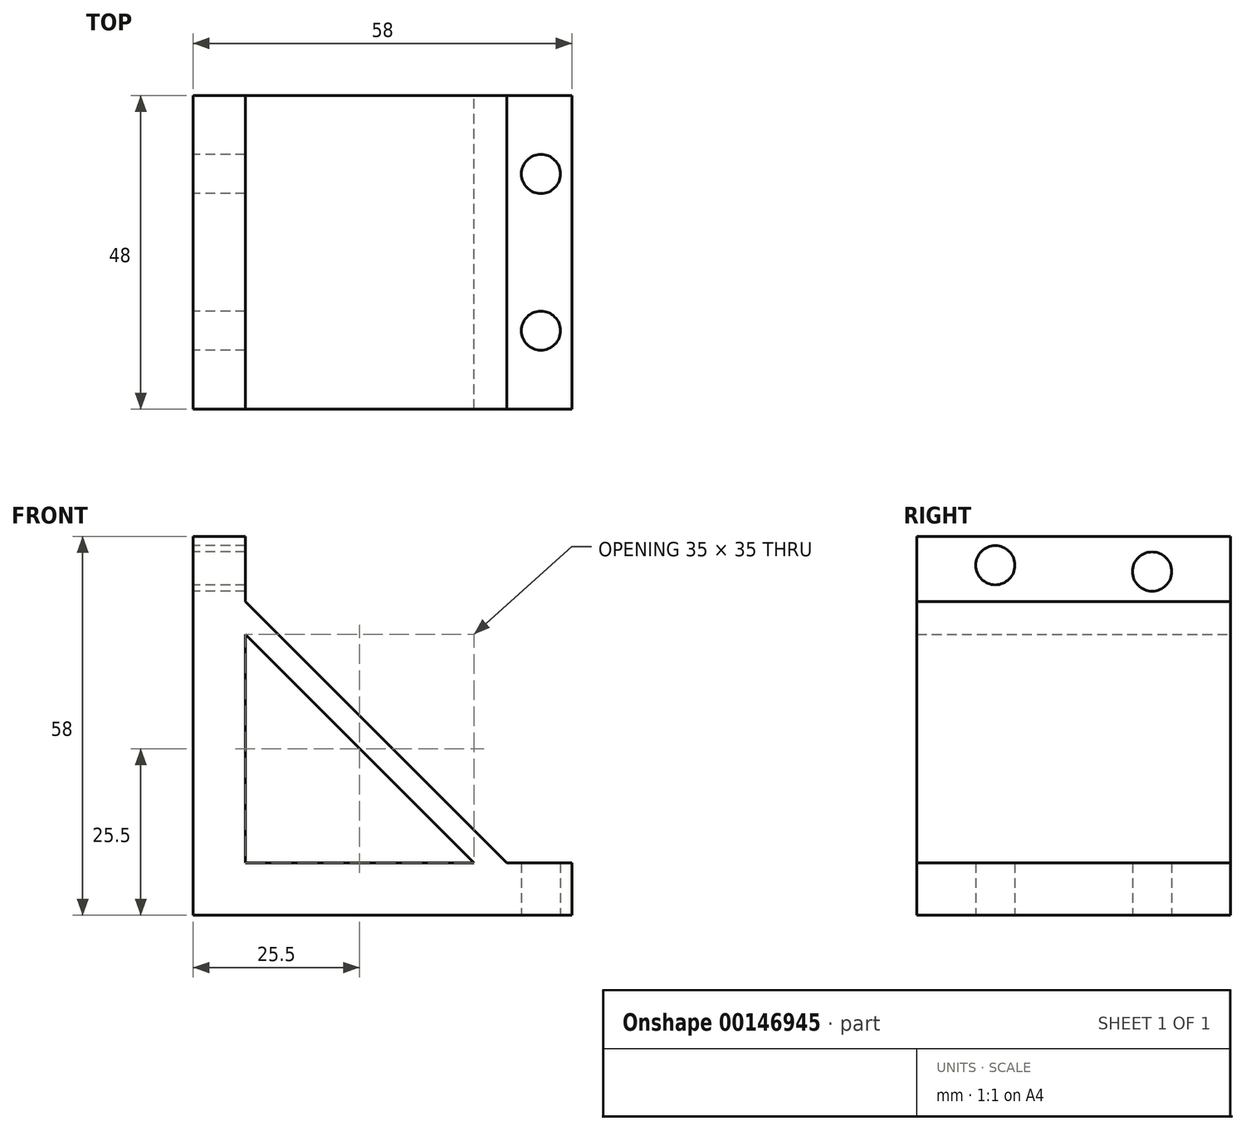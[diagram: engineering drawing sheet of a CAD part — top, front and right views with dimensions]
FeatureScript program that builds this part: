
annotation { "Feature Type Name" : "Feature", "Feature Type Description" : "" }
export const myFeature = defineFeature(function(context is Context, id is Id, definition is map)
    precondition{}
    {
        {
            var Q0;
            Q0=qCreatedBy(makeId("Front.planeOp"),FACE);
            var sketch = newSketch(context, id + "F0", { "sketchPlane" : qUnion([Q0])});
            skLineSegment(sketch, "E0", {"start": v(0, 0) * mm, "end": v(58, 0) * mm});
            skLineSegment(sketch, "E1", {"start": v(58, 0) * mm, "end": v(58, 8) * mm});
            skLineSegment(sketch, "E2", {"start": v(58, 8) * mm, "end": v(0, 8) * mm});
            skLineSegment(sketch, "E3", {"start": v(0, 8) * mm, "end": v(0, 0) * mm});
            skLineSegment(sketch, "E4", {"start": v(0, 8) * mm, "end": v(0, 58) * mm});
            skLineSegment(sketch, "E5", {"start": v(0, 58) * mm, "end": v(8, 58) * mm});
            skLineSegment(sketch, "E6", {"start": v(8, 58) * mm, "end": v(8, 8) * mm});
            skLineSegment(sketch, "E7", {"start": v(8, 43) * mm, "end": v(43, 8) * mm});
            skLineSegment(sketch, "E8", {"start": v(8, 48) * mm, "end": v(48, 8) * mm});
            skSolve(sketch);
        }
        {
            var Q0;
            Q0=makeQuery(id+"F0.imprint","IMPRINT",FACE,{"disambiguationData":[TD([[makeQuery(id+"F0.imprint","IMPRINT",EDGE,{"derivedFrom":sQuery(id+"F0.wireOp",EDGE,"E0")}),1.0]])]});
            var Q1;
            {var subQ0=sQuery(id+"F0.wireOp",EDGE,"E7");Q1=makeQuery(id+"F0.imprint","IMPRINT",FACE,{"disambiguationData":[TD([[makeQuery(id+"F0.imprint","IMPRINT",EDGE,{"derivedFrom":subQ0}),1.0]])]});}
            var Q2;
            {var subQ3=sQuery(id+"F0.wireOp",EDGE,"E4");Q2=makeQuery(id+"F0.imprint","IMPRINT",FACE,{"disambiguationData":[TD([[makeQuery(id+"F0.imprint","IMPRINT",EDGE,{"derivedFrom":subQ3}),-1.0]])]});}
            extrude(context, id + "F1", {"entities" : qUnion([Q0, Q1, Q2]), "depth" : 48 * mm});
        }
        {
            var Q0;
            Q0=qCreatedBy(makeId("Right.planeOp"),FACE);
            var sketch = newSketch(context, id + "F2", { "sketchPlane" : qUnion([Q0])});
            skLineSegment(sketch, "E9", {"start": v(-48, 53.6) * mm, "end": v(-36, 53.6) * mm, "construction": true});
            skCircle(sketch, "E10", {"center": v(-36, 53.6) * mm, "radius": 3 * mm});
            skLineSegment(sketch, "E11", {"start": v(0, 52.63) * mm, "end": v(-12, 52.63) * mm, "construction": true});
            skCircle(sketch, "E12", {"center": v(-12, 52.63) * mm, "radius": 3 * mm});
            skSolve(sketch);
        }
        {
            var Q0;
            Q0 = qSketchRegion(id + "F2", true);
            extrude(context, id + "F3", {"entities" : qUnion([Q0]), "operationType" : NewBodyOperationType.REMOVE, "depth" : 25 * mm});
        }
        {
            var Q0;
            Q0=qCreatedBy(makeId("Top.planeOp"),FACE);
            var sketch = newSketch(context, id + "F4", { "sketchPlane" : qUnion([Q0])});
            skLineSegment(sketch, "E13", {"start": v(53.23, 0) * mm, "end": v(53.23, -12) * mm, "construction": true});
            skLineSegment(sketch, "E14", {"start": v(53.23, -48) * mm, "end": v(53.23, -36) * mm, "construction": true});
            skPoint(sketch, "E14.startSnap0", {"position": v(53.23, -6) * mm});
            skCircle(sketch, "E15", {"center": v(53.23, -36) * mm, "radius": 3 * mm});
            skCircle(sketch, "E16", {"center": v(53.23, -12) * mm, "radius": 3 * mm});
            skSolve(sketch);
        }
        {
            var Q0;
            Q0 = qSketchRegion(id + "F4", true);
            extrude(context, id + "F5", {"entities" : qUnion([Q0]), "operationType" : NewBodyOperationType.REMOVE, "depth" : 25 * mm});
        }
    });
